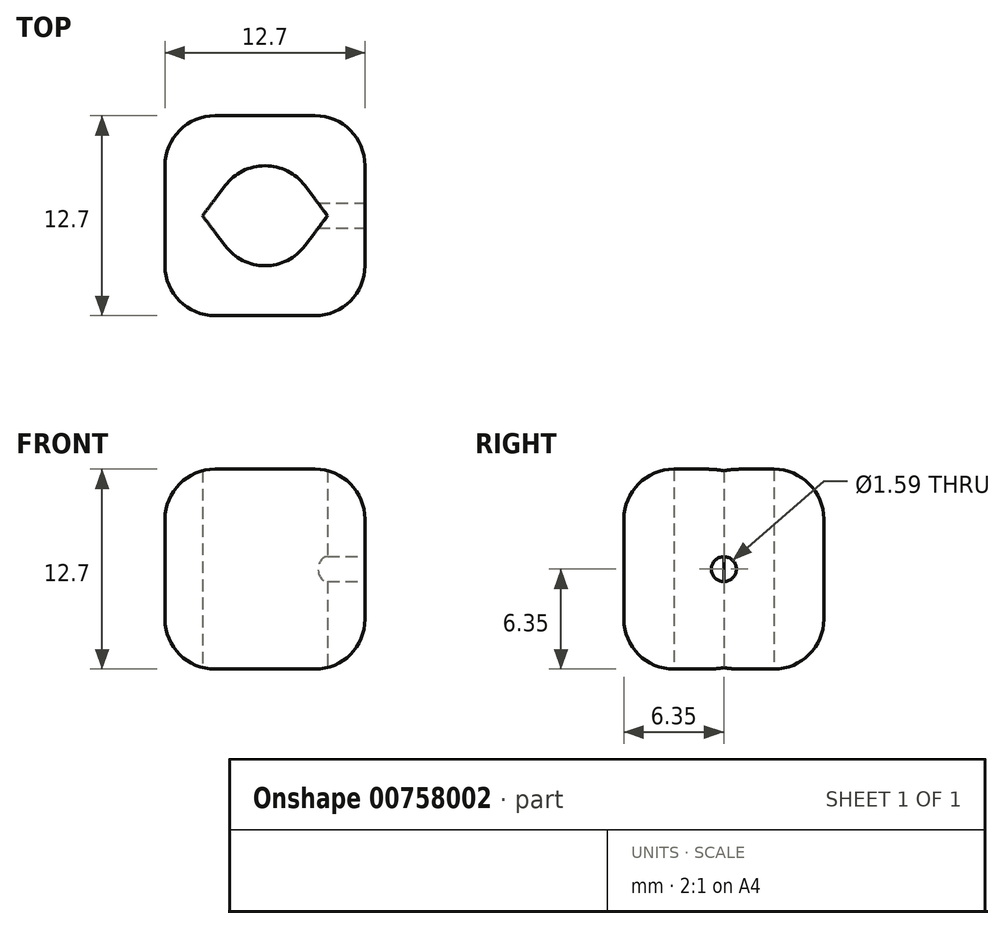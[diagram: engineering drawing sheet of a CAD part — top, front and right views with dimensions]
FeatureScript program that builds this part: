
annotation { "Feature Type Name" : "Feature", "Feature Type Description" : "" }
export const myFeature = defineFeature(function(context is Context, id is Id, definition is map)
    precondition{}
    {
        {
            var Q0;
            Q0=qCreatedBy(makeId("Top.planeOp"),FACE);
            var sketch = newSketch(context, id + "F0", { "sketchPlane" : qUnion([Q0])});
            skLineSegment(sketch, "E0.bottom", {"start": v(6.35, 6.35) * mm, "end": v(-6.35, 6.35) * mm});
            skLineSegment(sketch, "E0.top", {"start": v(6.35, -6.35) * mm, "end": v(-6.35, -6.35) * mm});
            skLineSegment(sketch, "E0.left", {"start": v(6.35, 6.35) * mm, "end": v(6.35, -6.35) * mm});
            skLineSegment(sketch, "E0.right", {"start": v(-6.35, 6.35) * mm, "end": v(-6.35, -6.35) * mm});
            skPoint(sketch, "E0.middle", {"position": v(0, 0) * mm});
            skCircle(sketch, "E1", {"center": v(0, 0) * mm, "radius": 3.18 * mm});
            skLineSegment(sketch, "E2", {"start": v(3.97, 0) * mm, "end": v(2.54, 1.9) * mm});
            skLineSegment(sketch, "E3", {"start": v(2.54, -1.9) * mm, "end": v(3.97, 0) * mm});
            skLineSegment(sketch, "E4", {"start": v(-3.97, 0) * mm, "end": v(-2.54, 1.9) * mm});
            skLineSegment(sketch, "E5", {"start": v(-3.97, 0) * mm, "end": v(-2.54, -1.9) * mm});
            skSolve(sketch);
        }
        {
            var Q0;
            Q0 = qSketchRegion(id + "F0", true);
            extrude(context, id + "F1", {"entities" : qUnion([Q0]), "depth" : 12.7 * mm, "offsetDistance" : 25.4 * mm});
        }
        {
            var Q0;
            Q0=makeQuery(id+"F1.opExtrude","SWEPT_EDGE",EDGE,{"disambiguationData":[OSD([sQuery(id+"F0.wireOp",EDGE,"E0.top"),sQuery(id+"F0.wireOp",EDGE,"E0.left")])]});
            var Q1;
            Q1=makeQuery(id+"F1.opExtrude","CAP_EDGE",EDGE,{"disambiguationData":[OSD([sQuery(id+"F0.wireOp",EDGE,"E0.top")])],"isStart":false});
            var Q2;
            Q2=makeQuery(id+"F1.opExtrude","CAP_EDGE",EDGE,{"disambiguationData":[OSD([sQuery(id+"F0.wireOp",EDGE,"E0.left")])],"isStart":false});
            var Q3;
            Q3=makeQuery(id+"F1.opExtrude","CAP_EDGE",EDGE,{"disambiguationData":[OSD([sQuery(id+"F0.wireOp",EDGE,"E0.left")])],"isStart":true});
            var Q4;
            Q4=makeQuery(id+"F1.opExtrude","CAP_EDGE",EDGE,{"disambiguationData":[OSD([sQuery(id+"F0.wireOp",EDGE,"E0.top")])],"isStart":true});
            var Q5;
            Q5=makeQuery(id+"F1.opExtrude","SWEPT_EDGE",EDGE,{"disambiguationData":[OSD([sQuery(id+"F0.wireOp",EDGE,"E0.bottom"),sQuery(id+"F0.wireOp",EDGE,"E0.left")])]});
            var Q6;
            Q6=makeQuery(id+"F1.opExtrude","CAP_EDGE",EDGE,{"disambiguationData":[OSD([sQuery(id+"F0.wireOp",EDGE,"E0.right")])],"isStart":true});
            var Q7;
            Q7=makeQuery(id+"F1.opExtrude","SWEPT_EDGE",EDGE,{"disambiguationData":[OSD([sQuery(id+"F0.wireOp",EDGE,"E0.bottom"),sQuery(id+"F0.wireOp",EDGE,"E0.right")])]});
            var Q8;
            Q8=makeQuery(id+"F1.opExtrude","CAP_EDGE",EDGE,{"disambiguationData":[OSD([sQuery(id+"F0.wireOp",EDGE,"E0.bottom")])],"isStart":true});
            var Q9;
            Q9=makeQuery(id+"F1.opExtrude","CAP_EDGE",EDGE,{"disambiguationData":[OSD([sQuery(id+"F0.wireOp",EDGE,"E0.bottom")])],"isStart":false});
            var Q10;
            Q10=makeQuery(id+"F1.opExtrude","CAP_EDGE",EDGE,{"disambiguationData":[OSD([sQuery(id+"F0.wireOp",EDGE,"E0.right")])],"isStart":false});
            var Q11;
            Q11=makeQuery(id+"F1.opExtrude","SWEPT_EDGE",EDGE,{"disambiguationData":[OSD([sQuery(id+"F0.wireOp",EDGE,"E0.top"),sQuery(id+"F0.wireOp",EDGE,"E0.right")])]});
            fillet(context, id + "F2", {"entities" : qUnion([Q0, Q1, Q2, Q3, Q4, Q5, Q6, Q7, Q8, Q9, Q10, Q11]), "radius" : 3.17 * mm, "tangentPropagation" : true, "allowEdgeOverflow" : false});
        }
        {
            var Q0;
            Q0=makeQuery(id+"F1.opExtrude","SWEPT_FACE",FACE,{"disambiguationData":[OSD([sQuery(id+"F0.wireOp",EDGE,"E0.left")])]});
            var sketch = newSketch(context, id + "F3", { "sketchPlane" : qUnion([Q0])});
            skCircle(sketch, "E6", {"center": v(0, 6.35) * mm, "radius": 0.8 * mm});
            skSolve(sketch);
        }
        {
            var Q0;
            Q0=makeQuery(id+"F3.imprint","IMPRINT",FACE,{"disambiguationData":[TD([[makeQuery(id+"F3.imprint","IMPRINT",EDGE,{"derivedFrom":sQuery(id+"F3.wireOp",EDGE,"E6")}),1.0]])]});
            extrude(context, id + "F4", {"entities" : qUnion([Q0]), "operationType" : NewBodyOperationType.REMOVE, "oppositeDirection" : true, "depth" : 6.3 * mm, "offsetDistance" : 25.4 * mm});
        }
    });
